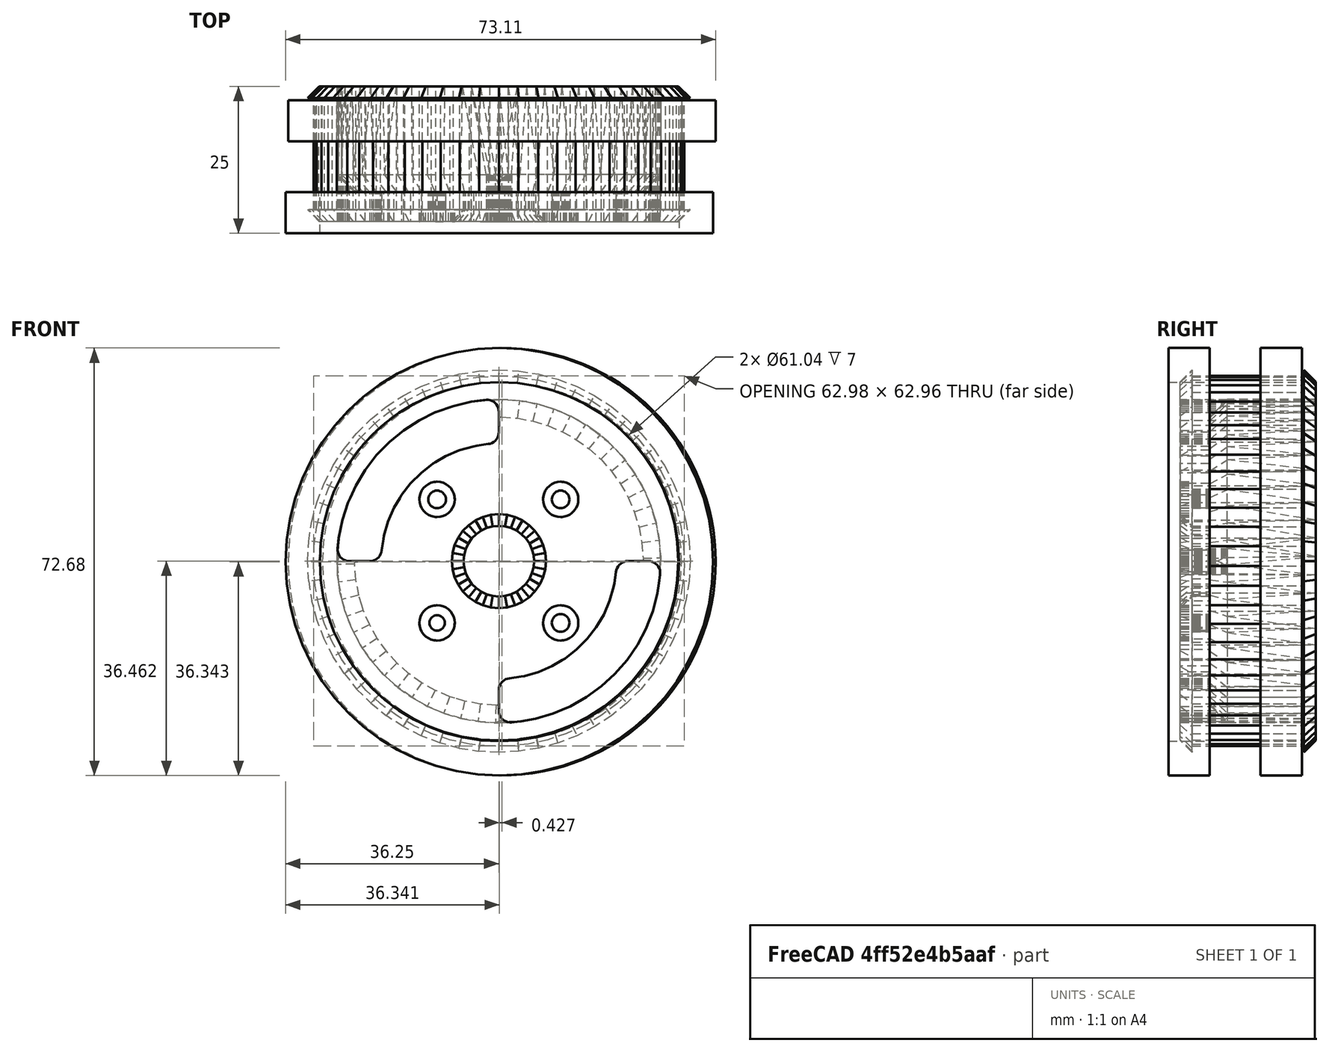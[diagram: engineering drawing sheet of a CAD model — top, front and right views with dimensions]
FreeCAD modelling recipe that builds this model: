
FCSTD DOCUMENT  (FreeCAD 1.0R39109 (Git))
Label: updated_wheel
License: All rights reserved
LicenseURL: https://en.wikipedia.org/wiki/All_rights_reserved
objects: Sketcher::SketchObject×4, PartDesign::Body×3, PartDesign::Pad×2, PartDesign::FeatureBase×1
note: 19 computed .brp shape members not serialized (recipe doc carries the construction recipe); baked Part::Feature solids carry a one-line shape summary decoded from their .brp

FEATURE [PartDesign::FeatureBase] BaseFeature
  Suppressed = false
FEATURE [PartDesign::Body] Body
  AllowCompound = false
  Group = -> [BaseFeature]
  Origin = -> Origin
  Tip = -> BaseFeature
FEATURE [Sketcher::SketchObject] Sketch
  ArcFitTolerance = 1e-06
  FullyConstrained = false
  MakeInternals = false
  MapMode = 5
  Placement = pos=(0,0,0) rot=(1,0,0;1.5708rad)
  sketch-geometry (2):
    g0: Circle CenterX=32.5913 CenterY=32.4034 CenterZ=0 NormalX=0 NormalY=0 NormalZ=1 AngleXU=0 Radius=36.3397
    g1: Circle CenterX=32.5913 CenterY=32.4034 CenterZ=0 NormalX=0 NormalY=0 NormalZ=1 AngleXU=0 Radius=30.5198
  constraints (1):
    c: Coincident(g1,g0)
FEATURE [Sketcher::SketchObject] Sketch001
  ArcFitTolerance = 1e-06
  FullyConstrained = false
  MakeInternals = false
  MapMode = 5
  Placement = pos=(0,0,0) rot=(1,0,0;1.5708rad)
  sketch-geometry (2):
    g0: Circle CenterX=32.5913 CenterY=32.4034 CenterZ=0 NormalX=0 NormalY=0 NormalZ=1 AngleXU=0 Radius=36.3397
    g1: Circle CenterX=32.5913 CenterY=32.4034 CenterZ=0 NormalX=0 NormalY=0 NormalZ=1 AngleXU=0 Radius=32.3544
  constraints (1):
    c: Coincident(g1,g0)
FEATURE [PartDesign::Pad] Pad
  Direction = (0,-1,2e-16)
  Length = 2
  Length2 = 5
  Placement = pos=(0,0,0) rot=(1,0,0;1.5708rad)
  Profile = -> Sketch
  ReferenceAxis = -> Sketch [N_Axis]
  Refine = true
  Suppressed = false
  Type = 4
FEATURE [PartDesign::Body] Body001
  AllowCompound = false
  Group = -> [Sketch,Pad,Sketch001]
  Origin = -> Origin001
  Tip = -> Pad
FEATURE [Sketcher::SketchObject] Sketch002
  ArcFitTolerance = 1e-06
  FullyConstrained = false
  MakeInternals = false
  MapMode = 5
  Placement = pos=(0,0,0) rot=(1,0,0;1.5708rad)
  sketch-geometry (2):
    g0: Circle CenterX=32.5913 CenterY=32.4034 CenterZ=0 NormalX=0 NormalY=0 NormalZ=1 AngleXU=0 Radius=36.3397
    g1: Circle CenterX=32.5913 CenterY=32.4034 CenterZ=0 NormalX=0 NormalY=0 NormalZ=1 AngleXU=0 Radius=30.5198
  constraints (1):
    c: Coincident(g1,g0)
FEATURE [PartDesign::Pad] Pad001
  Direction = (0,-1,0)
  Length = 2
  Length2 = 5
  Placement = pos=(0,0,0) rot=(1,0,0;1.5708rad)
  Profile = -> Sketch002
  ReferenceAxis = -> Sketch002 [N_Axis]
  Refine = true
  Suppressed = false
  Type = 4
FEATURE [Sketcher::SketchObject] Sketch003
  ArcFitTolerance = 1e-06
  FullyConstrained = false
  MakeInternals = false
  MapMode = 5
  Placement = pos=(0,0,0) rot=(1,0,0;1.5708rad)
  sketch-geometry (2):
    g0: Circle CenterX=32.5913 CenterY=32.4034 CenterZ=0 NormalX=0 NormalY=0 NormalZ=1 AngleXU=0 Radius=36.3397
    g1: Circle CenterX=32.5913 CenterY=32.4034 CenterZ=0 NormalX=0 NormalY=0 NormalZ=1 AngleXU=0 Radius=32.3544
  constraints (1):
    c: Coincident(g1,g0)
FEATURE [PartDesign::Body] Body002
  AllowCompound = false
  Group = -> [Sketch002,Pad001,Sketch003]
  Origin = -> Origin002
  Placement = pos=(0.427305,15.6458,0) rot=(0,0,1;0rad)
  Tip = -> Pad001
